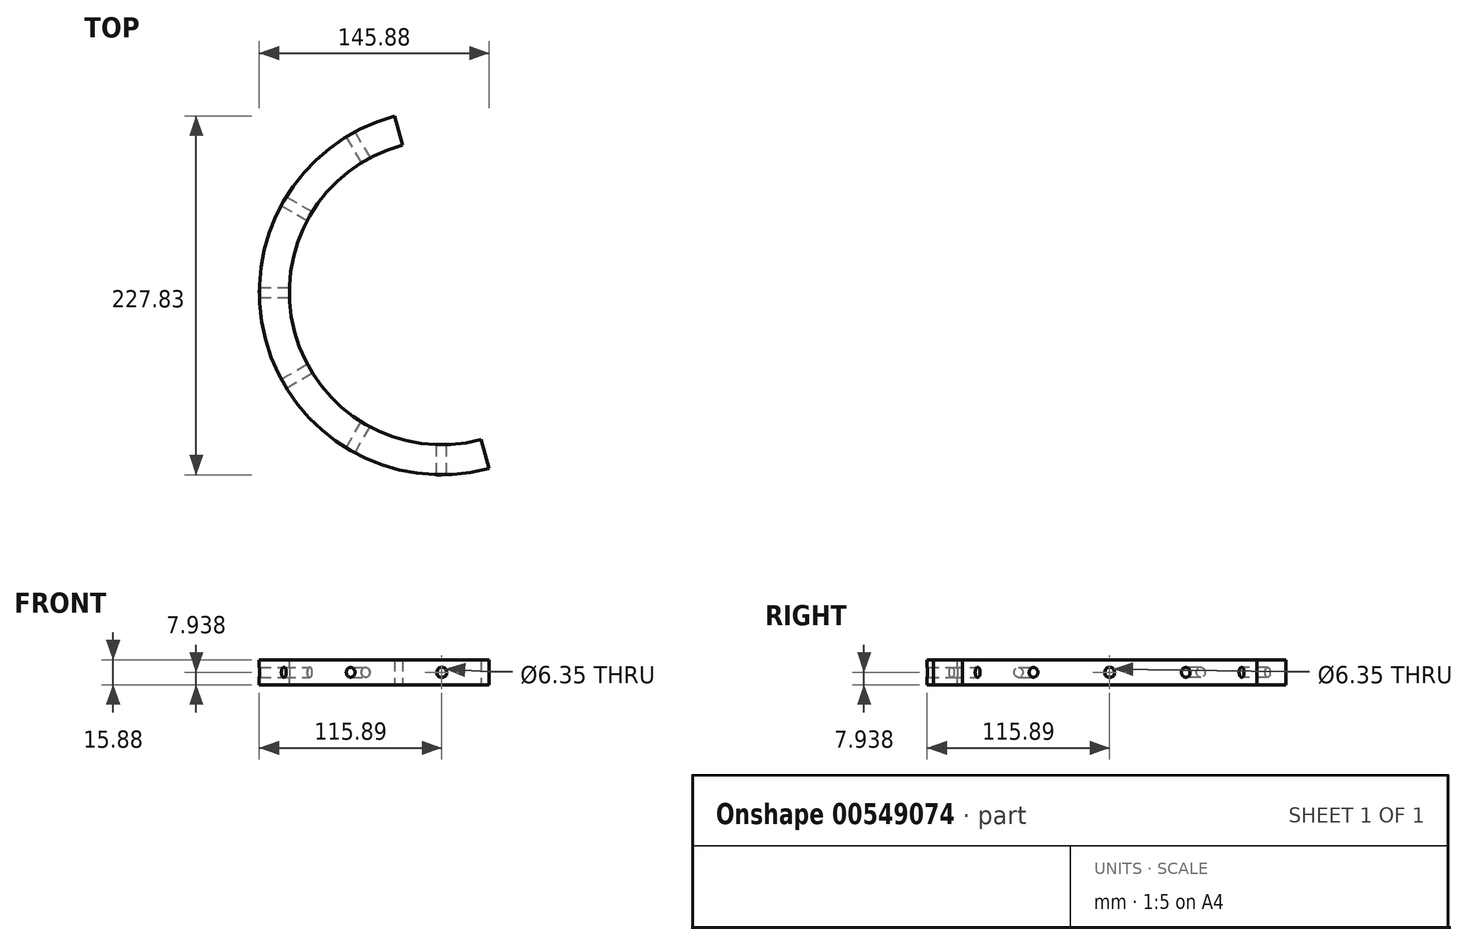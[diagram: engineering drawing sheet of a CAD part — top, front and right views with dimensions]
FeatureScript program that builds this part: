
annotation { "Feature Type Name" : "Feature", "Feature Type Description" : "" }
export const myFeature = defineFeature(function(context is Context, id is Id, definition is map)
    precondition{}
    {
        {
            var Q0;
            Q0=qCreatedBy(makeId("Top.planeOp"),FACE);
            var sketch = newSketch(context, id + "F0", { "sketchPlane" : qUnion([Q0])});
            skArc(sketch, "E0", {"start": v(-25.06, -93.54) * mm, "mid": v(0, -96.84) * mm, "end": v(25.06, -93.54) * mm});
            skArc(sketch, "E1", {"start": v(-30, -111.94) * mm, "mid": v(0, -115.89) * mm, "end": v(30, -111.94) * mm});
            skLineSegment(sketch, "E2", {"start": v(-25.06, -93.54) * mm, "end": v(-30, -111.94) * mm});
            skLineSegment(sketch, "E3", {"start": v(25.06, -93.54) * mm, "end": v(30, -111.94) * mm});
            skLineSegment(sketch, "E4", {"start": v(0, 0) * mm, "end": v(0, -85.96) * mm});
            skSolve(sketch);
        }
        {
            var Q0;
            Q0=makeQuery(id+"F0.imprint","IMPRINT",FACE,{"disambiguationData":[TD([[makeQuery(id+"F0.imprint","IMPRINT",EDGE,{"derivedFrom":sQuery(id+"F0.wireOp",EDGE,"E0")}),-1.0]])]});
            extrude(context, id + "F1", {"entities" : qUnion([Q0]), "depth" : 15.88 * mm, "offsetDistance" : 25.4 * mm});
        }
        {
            var Q0;
            Q0=qCreatedBy(makeId("Front.planeOp"),FACE);
            cPlane(context, id + "F2", {"entities" : qUnion([Q0]), "cplaneType" : CPlaneType.OFFSET, "offset" : 115.89 * mm, "width" : 152.4 * mm, "height" : 152.4 * mm});
        }
        {
            var Q0;
            Q0=qCreatedBy(id+"F2.planeOp",FACE);
            var sketch = newSketch(context, id + "F3", { "sketchPlane" : qUnion([Q0])});
            skPoint(sketch, "E5", {"position": v(0, 7.94) * mm});
            skLineSegment(sketch, "E6", {"start": v(0, 7.94) * mm, "end": v(-49.59, 7.94) * mm, "construction": true});
            skSolve(sketch);
        }
        {
            var Q0;
            Q0=sQuery(id+"F3.wireOp",VERTEX,"E5");
            var Q1;
            Q1=makeQuery(id+"F1.opExtrude","SWEPT_BODY",BODY,{"disambiguationData":[OSD([sQuery(id+"F0.wireOp",EDGE,"E0"),sQuery(id+"F0.wireOp",EDGE,"E1"),sQuery(id+"F0.wireOp",EDGE,"E2"),sQuery(id+"F0.wireOp",EDGE,"E3")])]});
            hole(context, id + "F4", {"style" : HoleStyle.SIMPLE, "endStyle" : HoleEndStyle.BLIND, "holeDiameter" : 6.35 * mm, "holeDepth" : 63.25 * mm, "isTappedThrough" : true, "tappedDepth" : 12.7 * mm, "tapClearance" : 3, "startFromSketch" : true, "locations" : qUnion([Q0]), "scope" : qUnion([Q1])});
        }
        {
            var Q0;
            Q0=makeQuery(id+"F1.opExtrude","SWEPT_BODY",BODY,{"disambiguationData":[OSD([sQuery(id+"F0.wireOp",EDGE,"E0"),sQuery(id+"F0.wireOp",EDGE,"E1"),sQuery(id+"F0.wireOp",EDGE,"E2"),sQuery(id+"F0.wireOp",EDGE,"E3")])]});
            var Q1;
            Q1=makeQuery(id+"F1.opExtrude","SWEPT_FACE",FACE,{"disambiguationData":[OSD([sQuery(id+"F0.wireOp",EDGE,"E1")])]});
            circularPattern(context, id + "F5", {"operationType" : NewBodyOperationType.ADD, "entities" : qUnion([Q0]), "axis" : qUnion([Q1]), "angle" : 150 * degree, "instanceCount" : 6, "equalSpace" : true});
        }
    });
